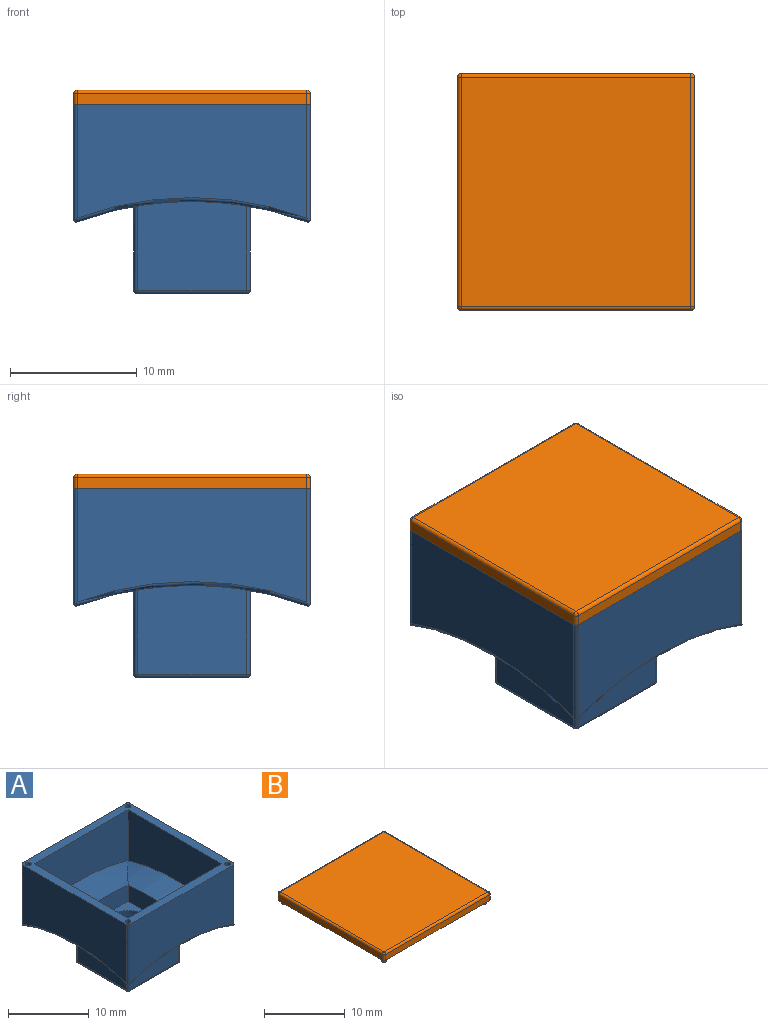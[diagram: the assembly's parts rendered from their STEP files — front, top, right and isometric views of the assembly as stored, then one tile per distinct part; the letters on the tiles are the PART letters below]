
ASSEMBLY  parts=2 mates=1
PART A: 56 faces, bbox 20.4x20.4x14.9 mm
  f0: plane 6.86x2.68mm, normal (0,-1,0), area 17.9mm2, adj f39,f41,f42,f53
  f1: plane 6.86x2.68mm, normal (0,1,0), area 17.9mm2, adj f33,f41,f42,f53
  f2: plane 18.14x8.94mm, normal (0,-1,0), area 142.6mm2, adj f6,f7,f31,f43
  f3: plane 18.14x8.94mm, normal (1,0,0), area 142.6mm2, adj f7,f9,f43,f55
  f4: plane 18.14x8.94mm, normal (0,1,0), area 142.6mm2, adj f8,f9,f32,f43
  f5: plane 18.14x8.94mm, normal (-1,0,0), area 142.6mm2, adj f6,f8,f43,f54
  f6: cylinder r=0.29mm len=9.24mm, axis (0,0,-1), area 4.2mm2, adj f2,f5,f31,f43,f54
  f7: cylinder r=0.29mm len=9.24mm, axis (0,0,1), area 4.2mm2, adj f2,f3,f31,f43,f55
  f8: cylinder r=0.29mm len=9.24mm, axis (0,0,1), area 4.2mm2, adj f4,f5,f32,f43,f54
  f9: cylinder r=0.29mm len=9.24mm, axis (0,0,-1), area 4.2mm2, adj f3,f4,f32,f43,f55
  f10: cylinder r=25.99mm len=18.14mm, axis (0,-1,0), area 62.2mm2, adj f11,f13,f17,f19,f24,f31
  f11: cylinder r=25.99mm len=18.14mm, axis (-1,0,0), area 62.2mm2, adj f10,f12,f14,f19,f21,f54
  f12: cylinder r=25.99mm len=18.14mm, axis (0,-1,0), area 62.2mm2, adj f11,f13,f15,f21,f30,f32
  f13: cylinder r=25.99mm len=18.14mm, axis (-1,0,0), area 62.2mm2, adj f10,f12,f16,f24,f30,f55
  f14: plane 8.61x7.04mm, normal (-1,0,0), area 59.5mm2, adj f11,f19,f21,f22
  f15: plane 8.61x7.04mm, normal (0,1,0), area 59.5mm2, adj f12,f21,f27,f30
  f16: plane 8.61x7.04mm, normal (1,0,0), area 59.5mm2, adj f13,f24,f28,f30
  f17: plane 8.61x7.04mm, normal (0,-1,0), area 59.5mm2, adj f10,f19,f23,f24
  f18: plane 8.61x8.61mm, normal (0,0,-1), area 47.5mm2, adj f22,f23,f27,f28,f52
  f19: cylinder r=0.29mm len=6.68mm, axis (0,0,1), area 3mm2, adj f10,f11,f14,f17,f20
  f20: sphere r=0.29mm, area 0.1mm2, adj f19,f22,f23
  f21: cylinder r=0.29mm len=6.68mm, axis (0,0,-1), area 3mm2, adj f11,f12,f14,f15,f25
  f22: cylinder r=0.29mm len=8.61mm, axis (0,-1,0), area 3.9mm2, adj f14,f18,f20,f25
  f23: cylinder r=0.29mm len=8.61mm, axis (1,0,0), area 3.9mm2, adj f17,f18,f20,f26
  f24: cylinder r=0.29mm len=6.68mm, axis (0,0,-1), area 3mm2, adj f10,f13,f16,f17,f26
  f25: sphere r=0.29mm, area 0.1mm2, adj f21,f22,f27
  f26: sphere r=0.29mm, area 0.1mm2, adj f23,f24,f28
  f27: cylinder r=0.29mm len=8.61mm, axis (-1,0,0), area 3.9mm2, adj f15,f18,f25,f29
  f28: cylinder r=0.29mm len=8.61mm, axis (0,1,0), area 3.9mm2, adj f16,f18,f26,f29
  f29: sphere r=0.29mm, area 0.1mm2, adj f27,f28,f30
  f30: cylinder r=0.29mm len=6.68mm, axis (0,0,1), area 3mm2, adj f12,f13,f15,f16,f29
  f31: torus R=26.29mm, axis (0,1,0), area 8.6mm2, adj f2,f6,f7,f10,f54,f55
  f32: torus R=26.29mm, axis (0,1,0), area 8.6mm2, adj f4,f8,f9,f12,f54,f55
  f33: cylinder r=27.16mm len=16.4mm, axis (0,-1,0), area 56.1mm2, adj f1,f34,f35,f40
  f34: cylinder r=27.16mm len=16.4mm, axis (-1,0,0), area 56.1mm2, adj f33,f38,f39,f41
  f35: plane 16.4x7.72mm, normal (0,1,0), area 112.7mm2, adj f33,f36,f38,f43
  f36: plane 16.4x7.72mm, normal (-1,0,0), area 112.7mm2, adj f35,f37,f40,f43
  f37: plane 16.4x7.72mm, normal (0,-1,0), area 112.7mm2, adj f36,f38,f39,f43
  f38: plane 16.4x7.72mm, normal (1,0,0), area 112.7mm2, adj f34,f35,f37,f43
  f39: cylinder r=27.16mm len=16.4mm, axis (0,-1,0), area 56.1mm2, adj f0,f34,f37,f40
  f40: cylinder r=27.16mm len=16.4mm, axis (-1,0,0), area 56.1mm2, adj f33,f36,f39,f42
  f41: plane 6.86x2.68mm, normal (1,0,0), area 17.9mm2, adj f0,f1,f34,f53
  f42: plane 6.86x2.68mm, normal (-1,0,0), area 17.9mm2, adj f0,f1,f40,f53
  f43: plane 18.73x18.73mm, normal (0,0,1), area 80mm2, adj f2,f3,f4,f5,f6,f7,f8,f9
  f44: cylinder r=0.36mm len=0.73mm, axis (0,0,1), area 1.7mm2, adj f43,f45
  f45: plane 0.73x0.73mm, normal (0,0,1), area 0.4mm2, adj f44
  f46: cylinder r=0.36mm len=0.73mm, axis (0,0,1), area 1.7mm2, adj f43,f47
  f47: plane 0.73x0.73mm, normal (0,0,1), area 0.4mm2, adj f46
  f48: cylinder r=0.36mm len=0.73mm, axis (0,0,1), area 1.7mm2, adj f43,f49
  f49: plane 0.73x0.73mm, normal (0,0,1), area 0.4mm2, adj f48
  f50: cylinder r=0.36mm len=0.73mm, axis (0,0,1), area 1.7mm2, adj f43,f51
  f51: plane 0.73x0.73mm, normal (0,0,1), area 0.4mm2, adj f50
  f52: cylinder r=2.91mm len=5.82mm, axis (0,0,-1), area 106.2mm2, adj f18,f53
  f53: plane 6.86x6.86mm, normal (0,0,1), area 20.5mm2, adj f0,f1,f41,f42,f52
  f54: torus R=26.29mm, axis (-1,0,0), area 8.6mm2, adj f5,f6,f8,f11,f31,f32
  f55: torus R=26.29mm, axis (-1,0,0), area 8.6mm2, adj f3,f7,f9,f13,f31,f32
PART B: 26 faces, bbox 18.7x18.7x1.7 mm
  f0: plane 18.73x18.73mm, normal (0,0,-1), area 349.5mm2, adj f10,f11,f12,f13,f14,f15,f16,f17
  f1: plane 18.14x18.14mm, normal (0,0,1), area 329.2mm2, adj f2,f3,f4,f5
  f2: cylinder r=0.29mm len=18.14mm, axis (1,0,0), area 8.3mm2, adj f1,f6,f7,f17
  f3: cylinder r=0.29mm len=18.14mm, axis (0,1,0), area 8.3mm2, adj f1,f7,f9,f16
  f4: cylinder r=0.29mm len=18.14mm, axis (-1,0,0), area 8.3mm2, adj f1,f8,f9,f14
  f5: cylinder r=0.29mm len=18.14mm, axis (0,-1,0), area 8.3mm2, adj f1,f6,f8,f13
  f6: sphere r=0.29mm, area 0.1mm2, adj f2,f5,f12
  f7: sphere r=0.29mm, area 0.1mm2, adj f2,f3,f15
  f8: sphere r=0.29mm, area 0.1mm2, adj f4,f5,f11
  f9: sphere r=0.29mm, area 0.1mm2, adj f3,f4,f10
  f10: cylinder r=0.29mm len=0.87mm, axis (0,0,-1), area 0.4mm2, adj f0,f9,f14,f16
  f11: cylinder r=0.29mm len=0.87mm, axis (0,0,1), area 0.4mm2, adj f0,f8,f13,f14
  f12: cylinder r=0.29mm len=0.87mm, axis (0,0,-1), area 0.4mm2, adj f0,f6,f13,f17
  f13: plane 18.14x0.87mm, normal (-1,0,0), area 15.8mm2, adj f0,f5,f11,f12
  f14: plane 18.14x0.87mm, normal (0,1,0), area 15.8mm2, adj f0,f4,f10,f11
  f15: cylinder r=0.29mm len=0.87mm, axis (0,0,1), area 0.4mm2, adj f0,f7,f16,f17
  f16: plane 18.14x0.87mm, normal (1,0,0), area 15.8mm2, adj f0,f3,f10,f15
  f17: plane 18.14x0.87mm, normal (0,-1,0), area 15.8mm2, adj f0,f2,f12,f15
  f18: cylinder r=0.29mm len=0.58mm, axis (0,0,1), area 1.1mm2, adj f0,f19
  f19: plane 0.58x0.58mm, normal (0,0,-1), area 0.3mm2, adj f18
  f20: cylinder r=0.29mm len=0.58mm, axis (0,0,1), area 1.1mm2, adj f0,f21
  f21: plane 0.58x0.58mm, normal (0,0,-1), area 0.3mm2, adj f20
  f22: cylinder r=0.29mm len=0.58mm, axis (0,0,1), area 1.1mm2, adj f0,f23
  f23: plane 0.58x0.58mm, normal (0,0,-1), area 0.3mm2, adj f22
  f24: cylinder r=0.29mm len=0.58mm, axis (0,0,1), area 1.1mm2, adj f0,f25
  f25: plane 0.58x0.58mm, normal (0,0,-1), area 0.3mm2, adj f24
PLACE A t=(-20.45,4.45,-19)mm
PLACE B t=(-49.79,4.45,-22.04)mm
MATE fastened B.f0 <-> A.f52  axis (0,0,-1) through (15.14,4.45,8.1)mm
